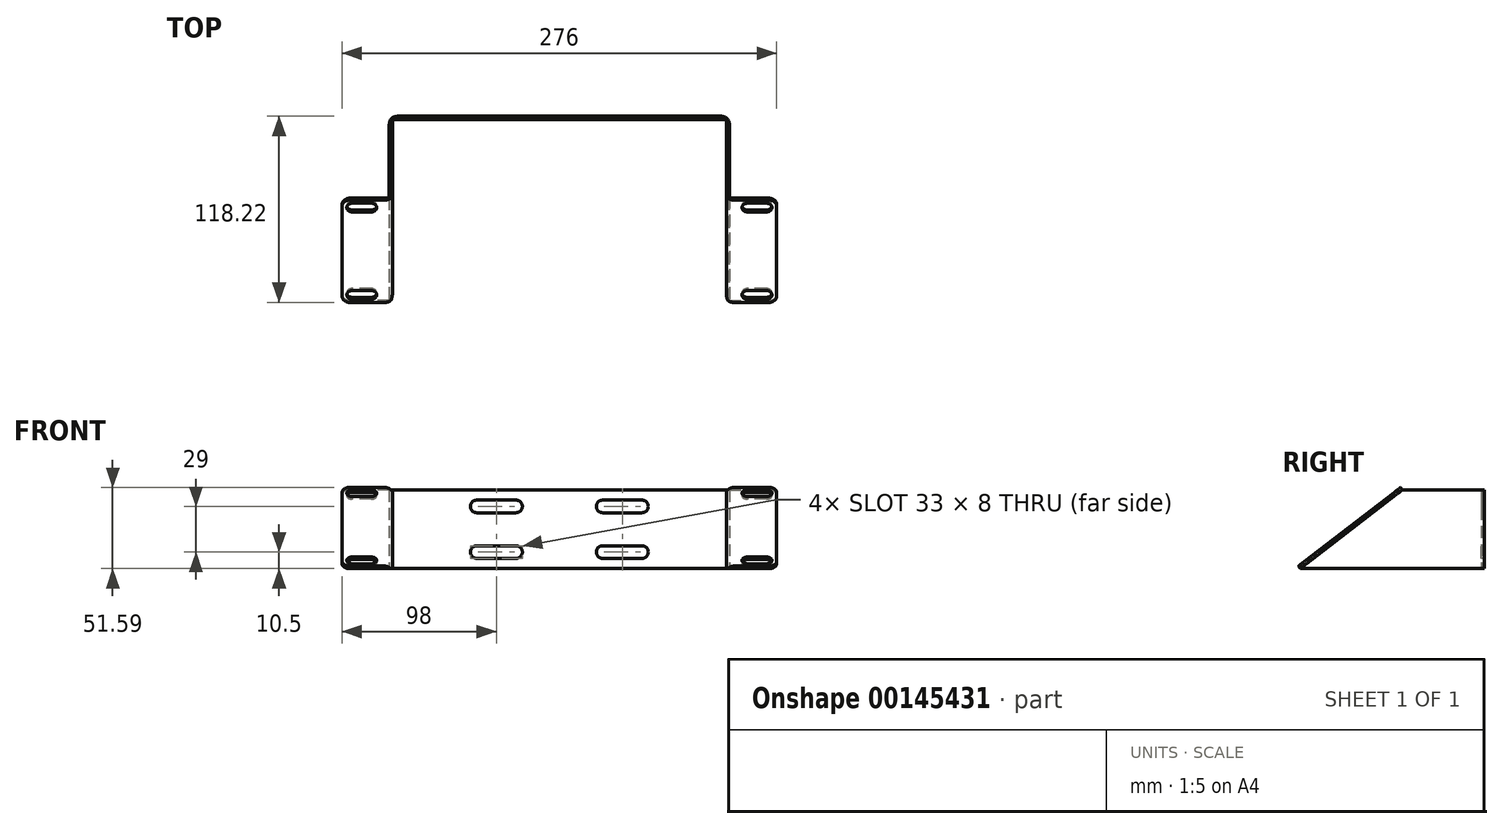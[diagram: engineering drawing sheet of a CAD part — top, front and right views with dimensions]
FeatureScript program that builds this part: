
annotation { "Feature Type Name" : "Feature", "Feature Type Description" : "" }
export const myFeature = defineFeature(function(context is Context, id is Id, definition is map)
    precondition{}
    {
        {
            var Q0;
            Q0=qCreatedBy(makeId("Front.planeOp"),FACE);
            var sketch = newSketch(context, id + "F0", { "sketchPlane" : qUnion([Q0])});
            skLineSegment(sketch, "E0.bottom", {"start": v(108, 25) * mm, "end": v(-108, 25) * mm});
            skLineSegment(sketch, "E0.top", {"start": v(108, -25) * mm, "end": v(-108, -25) * mm});
            skLineSegment(sketch, "E0.left", {"start": v(108, 25) * mm, "end": v(108, -25) * mm});
            skLineSegment(sketch, "E0.right", {"start": v(-108, 25) * mm, "end": v(-108, -25) * mm});
            skPoint(sketch, "E0.middle", {"position": v(0, 0) * mm});
            skCircle(sketch, "E1", {"center": v(-52.5, 14.5) * mm, "radius": 4 * mm});
            skCircle(sketch, "E2", {"center": v(-27.5, 14.5) * mm, "radius": 4 * mm});
            skLineSegment(sketch, "E3", {"start": v(-27.5, 18.5) * mm, "end": v(-52.5, 18.5) * mm});
            skLineSegment(sketch, "E4", {"start": v(-27.5, 10.5) * mm, "end": v(-52.5, 10.5) * mm});
            skCircle(sketch, "E5.MirrorC", {"center": v(-27.5, -14.5) * mm, "radius": 4 * mm});
            skLineSegment(sketch, "E6.MirrorCS", {"start": v(-27.5, -18.5) * mm, "end": v(-52.5, -18.5) * mm});
            skLineSegment(sketch, "E7.MirrorCS", {"start": v(-27.5, -10.5) * mm, "end": v(-52.5, -10.5) * mm});
            skCircle(sketch, "E8.MirrorC", {"center": v(-52.5, -14.5) * mm, "radius": 4 * mm});
            skCircle(sketch, "E9.MirrorC", {"center": v(27.5, 14.5) * mm, "radius": 4 * mm});
            skLineSegment(sketch, "E10.MirrorCS", {"start": v(27.5, 18.5) * mm, "end": v(52.5, 18.5) * mm});
            skLineSegment(sketch, "E11.MirrorCS", {"start": v(27.5, 10.5) * mm, "end": v(52.5, 10.5) * mm});
            skCircle(sketch, "E12.MirrorC", {"center": v(52.5, 14.5) * mm, "radius": 4 * mm});
            skLineSegment(sketch, "E13.MirrorCS", {"start": v(27.5, -10.5) * mm, "end": v(52.5, -10.5) * mm});
            skCircle(sketch, "E14.MirrorC", {"center": v(27.5, -14.5) * mm, "radius": 4 * mm});
            skLineSegment(sketch, "E15.MirrorCS", {"start": v(27.5, -18.5) * mm, "end": v(52.5, -18.5) * mm});
            skCircle(sketch, "E16.MirrorC", {"center": v(52.5, -14.5) * mm, "radius": 4 * mm});
            skSolve(sketch);
        }
        {
            var Q0;
            Q0 = qSketchRegion(id + "F0", true);
            extrude(context, id + "F1", {"entities" : qUnion([Q0]), "oppositeDirection" : true, "depth" : 2 * mm});
        }
        {
            var Q0;
            Q0=makeQuery(id+"F1.opExtrude","SWEPT_FACE",FACE,{"disambiguationData":[OSD([sQuery(id+"F0.wireOp",EDGE,"E0.right")])]});
            var sketch = newSketch(context, id + "F2", { "sketchPlane" : qUnion([Q0])});
            skLineSegment(sketch, "E17.bottom", {"start": v(0, -25) * mm, "end": v(115, -25) * mm});
            skLineSegment(sketch, "E17.top", {"start": v(0, 25) * mm, "end": v(50, 25) * mm});
            skLineSegment(sketch, "E17.left", {"start": v(0, -25) * mm, "end": v(0, 25) * mm});
            skPoint(sketch, "E18", {"position": v(50, 25) * mm});
            skLineSegment(sketch, "E19", {"start": v(50, 25) * mm, "end": v(115, -25) * mm});
            skSolve(sketch);
        }
        {
            var Q0;
            Q0 = qSketchRegion(id + "F2", true);
            extrude(context, id + "F3", {"entities" : qUnion([Q0]), "operationType" : NewBodyOperationType.ADD, "oppositeDirection" : true, "depth" : 2 * mm});
        }
        {
            var Q0;
            Q0=makeQuery(id+"F3.opExtrude","SWEPT_FACE",FACE,{"disambiguationData":[OSD([sQuery(id+"F2.wireOp",EDGE,"E19")])]});
            var sketch = newSketch(context, id + "F4", { "sketchPlane" : qUnion([Q0])});
            skLineSegment(sketch, "E20.bottom", {"start": v(-106, -24.39) * mm, "end": v(-138, -24.39) * mm});
            skLineSegment(sketch, "E20.top", {"start": v(-106, -106.4) * mm, "end": v(-138, -106.4) * mm});
            skLineSegment(sketch, "E20.left", {"start": v(-106, -24.39) * mm, "end": v(-106, -106.4) * mm});
            skLineSegment(sketch, "E20.right", {"start": v(-138, -24.39) * mm, "end": v(-138, -106.4) * mm});
            skCircle(sketch, "E21", {"center": v(-131.5, -30.4) * mm, "radius": 3.5 * mm});
            skCircle(sketch, "E22", {"center": v(-119.5, -30.4) * mm, "radius": 3.5 * mm});
            skLineSegment(sketch, "E23", {"start": v(-119.5, -26.9) * mm, "end": v(-131.5, -26.9) * mm});
            skLineSegment(sketch, "E24", {"start": v(-119.5, -33.9) * mm, "end": v(-131.5, -33.9) * mm});
            skLineSegment(sketch, "E25", {"start": v(-108, -65.4) * mm, "end": v(-146.48, -65.4) * mm, "construction": true});
            skCircle(sketch, "E26.MirrorC", {"center": v(-119.5, -100.4) * mm, "radius": 3.5 * mm});
            skLineSegment(sketch, "E27.MirrorCS", {"start": v(-119.5, -103.9) * mm, "end": v(-131.5, -103.9) * mm});
            skLineSegment(sketch, "E28.MirrorCS", {"start": v(-119.5, -96.9) * mm, "end": v(-131.5, -96.9) * mm});
            skCircle(sketch, "E29.MirrorC", {"center": v(-131.5, -100.4) * mm, "radius": 3.5 * mm});
            skSolve(sketch);
        }
        {
            var Q0;
            Q0 = qSketchRegion(id + "F4", true);
            extrude(context, id + "F5", {"entities" : qUnion([Q0]), "operationType" : NewBodyOperationType.ADD, "depth" : 2 * mm});
        }
        {
            var Q0;
            Q0=makeQuery(id+"F1.opExtrude","SWEPT_FACE",FACE,{"disambiguationData":[OSD([sQuery(id+"F0.wireOp",EDGE,"E0.left")])]});
            var sketch = newSketch(context, id + "F6", { "sketchPlane" : qUnion([Q0])});
            skLineSegment(sketch, "E30", {"start": v(0, 25) * mm, "end": v(-50, 25) * mm});
            skLineSegment(sketch, "E31", {"start": v(0, -25) * mm, "end": v(-115, -25) * mm});
            skLineSegment(sketch, "E32", {"start": v(-115, -25) * mm, "end": v(-50, 25) * mm});
            skLineSegment(sketch, "E33", {"start": v(0, 25) * mm, "end": v(0, -25) * mm});
            skSolve(sketch);
        }
        {
            var Q0;
            Q0 = qSketchRegion(id + "F6", true);
            extrude(context, id + "F7", {"entities" : qUnion([Q0]), "operationType" : NewBodyOperationType.ADD, "oppositeDirection" : true, "depth" : 2 * mm});
        }
        {
            var Q0;
            Q0=makeQuery(id+"F7.opExtrude","SWEPT_FACE",FACE,{"disambiguationData":[OSD([sQuery(id+"F6.wireOp",EDGE,"E32")])]});
            var sketch = newSketch(context, id + "F8", { "sketchPlane" : qUnion([Q0])});
            skLineSegment(sketch, "E34", {"start": v(106, -24.39) * mm, "end": v(138, -24.39) * mm});
            skLineSegment(sketch, "E35", {"start": v(138, -24.39) * mm, "end": v(138, -106.4) * mm});
            skLineSegment(sketch, "E36", {"start": v(138, -106.4) * mm, "end": v(106, -106.4) * mm});
            skLineSegment(sketch, "E37", {"start": v(106, -106.4) * mm, "end": v(106, -24.39) * mm});
            skCircle(sketch, "E38", {"center": v(119.5, -30.4) * mm, "radius": 3.5 * mm});
            skCircle(sketch, "E39", {"center": v(131.5, -30.4) * mm, "radius": 3.5 * mm});
            skLineSegment(sketch, "E40", {"start": v(131.5, -26.9) * mm, "end": v(119.5, -26.9) * mm});
            skLineSegment(sketch, "E41", {"start": v(131.5, -33.9) * mm, "end": v(119.5, -33.9) * mm});
            skLineSegment(sketch, "E42", {"start": v(108, -65.4) * mm, "end": v(160.8, -65.4) * mm, "construction": true});
            skPoint(sketch, "E42.endSnap0", {"position": v(108, -65.4) * mm});
            skCircle(sketch, "E43.MirrorC", {"center": v(131.5, -100.4) * mm, "radius": 3.5 * mm});
            skLineSegment(sketch, "E44.MirrorCS", {"start": v(131.5, -103.9) * mm, "end": v(119.5, -103.9) * mm});
            skLineSegment(sketch, "E45.MirrorCS", {"start": v(131.5, -96.9) * mm, "end": v(119.5, -96.9) * mm});
            skCircle(sketch, "E46.MirrorC", {"center": v(119.5, -100.4) * mm, "radius": 3.5 * mm});
            skSolve(sketch);
        }
        {
            var Q0;
            Q0 = qSketchRegion(id + "F8", true);
            extrude(context, id + "F9", {"entities" : qUnion([Q0]), "operationType" : NewBodyOperationType.ADD, "depth" : 2 * mm});
        }
        {
            var Q0;
            Q0=makeQuery(id+"F5.opExtrude","CAP_EDGE",EDGE,{"disambiguationData":[OSD([sQuery(id+"F4.wireOp",EDGE,"E20.left")])],"isStart":false});
            var Q1;
            Q1=makeQuery(id+"F3.opExtrude","CAP_EDGE",EDGE,{"disambiguationData":[OSD([sQuery(id+"F2.wireOp",EDGE,"E19")])],"isStart":true});
            var Q2;
            Q2=makeQuery(id+"F1.opExtrude","CAP_EDGE",EDGE,{"disambiguationData":[OSD([sQuery(id+"F0.wireOp",EDGE,"E0.right")])],"isStart":false});
            var Q3;
            Q3=makeQuery(id+"F3.opExtrude","CAP_EDGE",EDGE,{"disambiguationData":[OSD([sQuery(id+"F2.wireOp",EDGE,"E17.left")])],"isStart":false});
            var Q4;
            Q4=makeQuery(id+"F7.opExtrude","CAP_EDGE",EDGE,{"disambiguationData":[OSD([sQuery(id+"F6.wireOp",EDGE,"E33")])],"isStart":false});
            var Q5;
            Q5=makeQuery(id+"F1.opExtrude","CAP_EDGE",EDGE,{"disambiguationData":[OSD([sQuery(id+"F0.wireOp",EDGE,"E0.left")])],"isStart":false});
            var Q6;
            Q6=makeQuery(id+"F7.opExtrude","CAP_EDGE",EDGE,{"disambiguationData":[OSD([sQuery(id+"F6.wireOp",EDGE,"E32")])],"isStart":true});
            var Q7;
            Q7=makeQuery(id+"F9.opExtrude","CAP_EDGE",EDGE,{"disambiguationData":[OSD([sQuery(id+"F8.wireOp",EDGE,"7c8a4223-fe46-4f25-9799-4720f2f076be.MirrorCS")])],"isStart":false});
            var Q8;
            Q8=makeQuery(id+"F9.opExtrude","SWEPT_EDGE",EDGE,{"disambiguationData":[OSD([sQuery(id+"F8.wireOp",EDGE,"4f635e31-f5a9-4145-95e6-9406a59558ed.MirrorCS"),sQuery(id+"F8.wireOp",EDGE,"16c7faa9-be56-412e-b69e-ab0ac4f993fc.MirrorCS")])]});
            var Q9;
            Q9=makeQuery(id+"F9.opExtrude","SWEPT_EDGE",EDGE,{"disambiguationData":[OSD([sQuery(id+"F8.wireOp",EDGE,"33cb2207-38b8-4227-a14b-f56ed14e0e1c.MirrorCS"),sQuery(id+"F8.wireOp",EDGE,"16c7faa9-be56-412e-b69e-ab0ac4f993fc.MirrorCS")])]});
            var Q10;
            Q10=makeQuery(id+"F5.opExtrude","SWEPT_EDGE",EDGE,{"disambiguationData":[OSD([sQuery(id+"F4.wireOp",EDGE,"E20.top"),sQuery(id+"F4.wireOp",EDGE,"E20.right")])]});
            var Q11;
            Q11=makeQuery(id+"F5.opExtrude","SWEPT_EDGE",EDGE,{"disambiguationData":[OSD([sQuery(id+"F4.wireOp",EDGE,"E20.bottom"),sQuery(id+"F4.wireOp",EDGE,"E20.right")])]});
            var Q12;
            Q12=makeQuery(id+"F9.opExtrude","CAP_EDGE",EDGE,{"disambiguationData":[OSD([sQuery(id+"F8.wireOp",EDGE,"E37")])],"isStart":false});
            var Q13;
            Q13=makeQuery(id+"F9.opExtrude","SWEPT_EDGE",EDGE,{"disambiguationData":[OSD([sQuery(id+"F8.wireOp",EDGE,"E34"),sQuery(id+"F8.wireOp",EDGE,"E35")])]});
            var Q14;
            Q14=makeQuery(id+"F9.opExtrude","SWEPT_EDGE",EDGE,{"disambiguationData":[OSD([sQuery(id+"F8.wireOp",EDGE,"E35"),sQuery(id+"F8.wireOp",EDGE,"E36")])]});
            fillet(context, id + "F10", {"entities" : qUnion([Q0, Q1, Q2, Q3, Q4, Q5, Q6, Q7, Q8, Q9, Q10, Q11, Q12, Q13, Q14]), "radius" : 5 * mm, "tangentPropagation" : true, "allowEdgeOverflow" : false});
        }
    });
